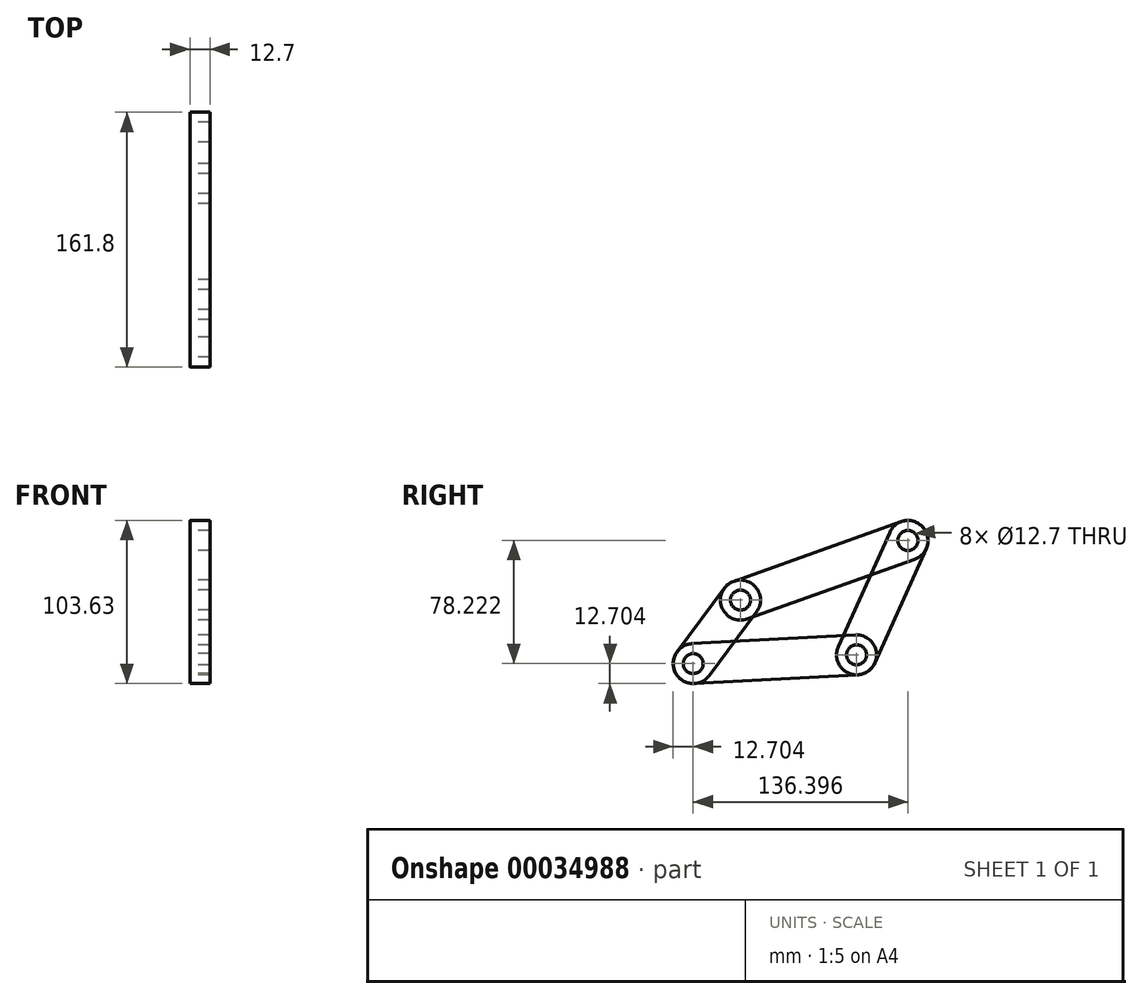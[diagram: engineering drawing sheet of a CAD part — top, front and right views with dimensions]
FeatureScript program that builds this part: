
annotation { "Feature Type Name" : "Feature", "Feature Type Description" : "" }
export const myFeature = defineFeature(function(context is Context, id is Id, definition is map)
    precondition{}
    {
        {
            var Q0;
            Q0=qCreatedBy(makeId("Right.planeOp"),FACE);
            var sketch = newSketch(context, id + "F0", { "sketchPlane" : qUnion([Q0])});
            skCircle(sketch, "E0", {"center": v(0, 0) * mm, "radius": 6.35 * mm});
            skCircle(sketch, "E1", {"center": v(0, 0) * mm, "radius": 12.7 * mm});
            skCircle(sketch, "E2", {"center": v(32.64, 72.66) * mm, "radius": 6.35 * mm});
            skCircle(sketch, "E3", {"center": v(32.64, 72.66) * mm, "radius": 12.7 * mm});
            skCircle(sketch, "E4", {"center": v(-73.72, 34.76) * mm, "radius": 6.35 * mm});
            skCircle(sketch, "E5", {"center": v(-73.72, 34.76) * mm, "radius": 12.7 * mm});
            skCircle(sketch, "E6", {"center": v(-103.76, -5.57) * mm, "radius": 6.35 * mm});
            skCircle(sketch, "E7", {"center": v(-103.76, -5.57) * mm, "radius": 12.7 * mm});
            skLineSegment(sketch, "E8", {"start": v(-104.44, 7.12) * mm, "end": v(-0.68, 12.68) * mm});
            skLineSegment(sketch, "E9", {"start": v(11.58, -5.2) * mm, "end": v(44.22, 67.45) * mm});
            skLineSegment(sketch, "E10", {"start": v(28.38, 84.62) * mm, "end": v(-77.99, 46.72) * mm});
            skLineSegment(sketch, "E11", {"start": v(-83.9, 42.35) * mm, "end": v(-113.94, 2.02) * mm});
            skLineSegment(sketch, "E12", {"start": v(-103.08, -18.25) * mm, "end": v(0.68, -12.68) * mm});
            skLineSegment(sketch, "E13", {"start": v(21.06, 77.86) * mm, "end": v(-11.58, 5.2) * mm});
            skLineSegment(sketch, "E14", {"start": v(-69.46, 22.8) * mm, "end": v(36.9, 60.7) * mm});
            skLineSegment(sketch, "E15", {"start": v(-63.54, 27.18) * mm, "end": v(-93.57, -13.15) * mm});
            skSolve(sketch);
        }
        {
            var Q0;
            Q0=makeQuery(id+"F0.imprint","IMPRINT",FACE,{"disambiguationData":[TD([[makeQuery(id+"F0.imprint","IMPRINT",EDGE,{"derivedFrom":sQuery(id+"F0.wireOp",EDGE,"E4")}),-1.0]])]});
            var Q1;
            {var subQ7=sQuery(id+"F0.wireOp",EDGE,"E11");Q1=makeQuery(id+"F0.imprint","IMPRINT",FACE,{"disambiguationData":[TD([[makeQuery(id+"F0.imprint","IMPRINT",EDGE,{"derivedFrom":subQ7}),1.0]])]});}
            var Q2;
            {var subQ1=sQuery(id+"F0.wireOp",EDGE,"E14");var subQ3=sQuery(id+"F0.wireOp",EDGE,"E5");var subQ5=makeQuery(id+"F0.imprint","INTERSECT",VERTEX,{"derivedFrom":[subQ3,subQ1]});Q2=makeQuery(id+"F0.imprint","IMPRINT",FACE,{"disambiguationData":[TD([[makeQuery(id+"F0.imprint","IMPRINT",EDGE,{"disambiguationData":[TD([[subQ5,-1.0]])],"derivedFrom":subQ3}),-1.0]])]});}
            var Q3;
            {var subQ1=sQuery(id+"F0.wireOp",EDGE,"E8");var subQ3=sQuery(id+"F0.wireOp",EDGE,"E7");var subQ5=makeQuery(id+"F0.imprint","INTERSECT",VERTEX,{"derivedFrom":[subQ3,subQ1]});Q3=makeQuery(id+"F0.imprint","IMPRINT",FACE,{"disambiguationData":[TD([[makeQuery(id+"F0.imprint","IMPRINT",EDGE,{"disambiguationData":[TD([[subQ5,1.0]])],"derivedFrom":subQ3}),-1.0]])]});}
            var Q4;
            Q4=makeQuery(id+"F0.imprint","IMPRINT",FACE,{"disambiguationData":[TD([[makeQuery(id+"F0.imprint","IMPRINT",EDGE,{"derivedFrom":sQuery(id+"F0.wireOp",EDGE,"E6")}),-1.0]])]});
            extrude(context, id + "F1", {"entities" : qUnion([Q0, Q1, Q2, Q3, Q4]), "depth" : 12.7 * mm});
        }
        {
            var Q0;
            {var subQ1=sQuery(id+"F0.wireOp",EDGE,"E13");var subQ3=sQuery(id+"F0.wireOp",EDGE,"E3");var subQ5=makeQuery(id+"F0.imprint","INTERSECT",VERTEX,{"derivedFrom":[subQ3,subQ1]});Q0=makeQuery(id+"F0.imprint","IMPRINT",FACE,{"disambiguationData":[TD([[makeQuery(id+"F0.imprint","IMPRINT",EDGE,{"disambiguationData":[TD([[subQ5,-1.0]])],"derivedFrom":subQ3}),-1.0]])]});}
            var Q1;
            {var subQ7=sQuery(id+"F0.wireOp",EDGE,"E9");Q1=makeQuery(id+"F0.imprint","IMPRINT",FACE,{"disambiguationData":[TD([[makeQuery(id+"F0.imprint","IMPRINT",EDGE,{"derivedFrom":subQ7}),1.0]])]});}
            var Q2;
            Q2=makeQuery(id+"F0.imprint","IMPRINT",FACE,{"disambiguationData":[TD([[makeQuery(id+"F0.imprint","IMPRINT",EDGE,{"derivedFrom":sQuery(id+"F0.wireOp",EDGE,"E2")}),-1.0]])]});
            var Q3;
            {var subQ1=sQuery(id+"F0.wireOp",EDGE,"E8");var subQ3=sQuery(id+"F0.wireOp",EDGE,"E1");var subQ5=makeQuery(id+"F0.imprint","INTERSECT",VERTEX,{"derivedFrom":[subQ3,subQ1]});Q3=makeQuery(id+"F0.imprint","IMPRINT",FACE,{"disambiguationData":[TD([[makeQuery(id+"F0.imprint","IMPRINT",EDGE,{"disambiguationData":[TD([[subQ5,-1.0]])],"derivedFrom":subQ3}),-1.0]])]});}
            var Q4;
            Q4=makeQuery(id+"F0.imprint","IMPRINT",FACE,{"disambiguationData":[TD([[makeQuery(id+"F0.imprint","IMPRINT",EDGE,{"derivedFrom":sQuery(id+"F0.wireOp",EDGE,"E0")}),-1.0]])]});
            extrude(context, id + "F2", {"entities" : qUnion([Q0, Q1, Q2, Q3, Q4]), "depth" : 12.7 * mm});
        }
        {
            var Q0;
            Q0=makeQuery(id+"F0.imprint","IMPRINT",FACE,{"disambiguationData":[TD([[makeQuery(id+"F0.imprint","IMPRINT",EDGE,{"derivedFrom":sQuery(id+"F0.wireOp",EDGE,"E4")}),-1.0]])]});
            var Q1;
            {var subQ7=sQuery(id+"F0.wireOp",EDGE,"E10");Q1=makeQuery(id+"F0.imprint","IMPRINT",FACE,{"disambiguationData":[TD([[makeQuery(id+"F0.imprint","IMPRINT",EDGE,{"derivedFrom":subQ7}),1.0]])]});}
            var Q2;
            {var subQ1=sQuery(id+"F0.wireOp",EDGE,"E13");var subQ3=sQuery(id+"F0.wireOp",EDGE,"E3");var subQ5=makeQuery(id+"F0.imprint","INTERSECT",VERTEX,{"derivedFrom":[subQ3,subQ1]});Q2=makeQuery(id+"F0.imprint","IMPRINT",FACE,{"disambiguationData":[TD([[makeQuery(id+"F0.imprint","IMPRINT",EDGE,{"disambiguationData":[TD([[subQ5,-1.0]])],"derivedFrom":subQ3}),-1.0]])]});}
            var Q3;
            Q3=makeQuery(id+"F0.imprint","IMPRINT",FACE,{"disambiguationData":[TD([[makeQuery(id+"F0.imprint","IMPRINT",EDGE,{"derivedFrom":sQuery(id+"F0.wireOp",EDGE,"E2")}),-1.0]])]});
            var Q4;
            {var subQ1=sQuery(id+"F0.wireOp",EDGE,"E14");var subQ3=sQuery(id+"F0.wireOp",EDGE,"E5");var subQ5=makeQuery(id+"F0.imprint","INTERSECT",VERTEX,{"derivedFrom":[subQ3,subQ1]});Q4=makeQuery(id+"F0.imprint","IMPRINT",FACE,{"disambiguationData":[TD([[makeQuery(id+"F0.imprint","IMPRINT",EDGE,{"disambiguationData":[TD([[subQ5,-1.0]])],"derivedFrom":subQ3}),-1.0]])]});}
            extrude(context, id + "F3", {"entities" : qUnion([Q0, Q1, Q2, Q3, Q4]), "depth" : 12.7 * mm});
        }
        {
            var Q0;
            Q0=makeQuery(id+"F0.imprint","IMPRINT",FACE,{"disambiguationData":[TD([[makeQuery(id+"F0.imprint","IMPRINT",EDGE,{"derivedFrom":sQuery(id+"F0.wireOp",EDGE,"E6")}),-1.0]])]});
            var Q1;
            {var subQ9=sQuery(id+"F0.wireOp",EDGE,"E12");Q1=makeQuery(id+"F0.imprint","IMPRINT",FACE,{"disambiguationData":[TD([[makeQuery(id+"F0.imprint","IMPRINT",EDGE,{"derivedFrom":subQ9}),1.0]])]});}
            var Q2;
            {var subQ1=sQuery(id+"F0.wireOp",EDGE,"E8");var subQ3=sQuery(id+"F0.wireOp",EDGE,"E1");var subQ5=makeQuery(id+"F0.imprint","INTERSECT",VERTEX,{"derivedFrom":[subQ3,subQ1]});Q2=makeQuery(id+"F0.imprint","IMPRINT",FACE,{"disambiguationData":[TD([[makeQuery(id+"F0.imprint","IMPRINT",EDGE,{"disambiguationData":[TD([[subQ5,-1.0]])],"derivedFrom":subQ3}),-1.0]])]});}
            var Q3;
            Q3=makeQuery(id+"F0.imprint","IMPRINT",FACE,{"disambiguationData":[TD([[makeQuery(id+"F0.imprint","IMPRINT",EDGE,{"derivedFrom":sQuery(id+"F0.wireOp",EDGE,"E0")}),-1.0]])]});
            var Q4;
            {var subQ1=sQuery(id+"F0.wireOp",EDGE,"E8");var subQ3=sQuery(id+"F0.wireOp",EDGE,"E7");var subQ5=makeQuery(id+"F0.imprint","INTERSECT",VERTEX,{"derivedFrom":[subQ3,subQ1]});Q4=makeQuery(id+"F0.imprint","IMPRINT",FACE,{"disambiguationData":[TD([[makeQuery(id+"F0.imprint","IMPRINT",EDGE,{"disambiguationData":[TD([[subQ5,1.0]])],"derivedFrom":subQ3}),-1.0]])]});}
            extrude(context, id + "F4", {"entities" : qUnion([Q0, Q1, Q2, Q3, Q4]), "depth" : 12.7 * mm});
        }
    });
